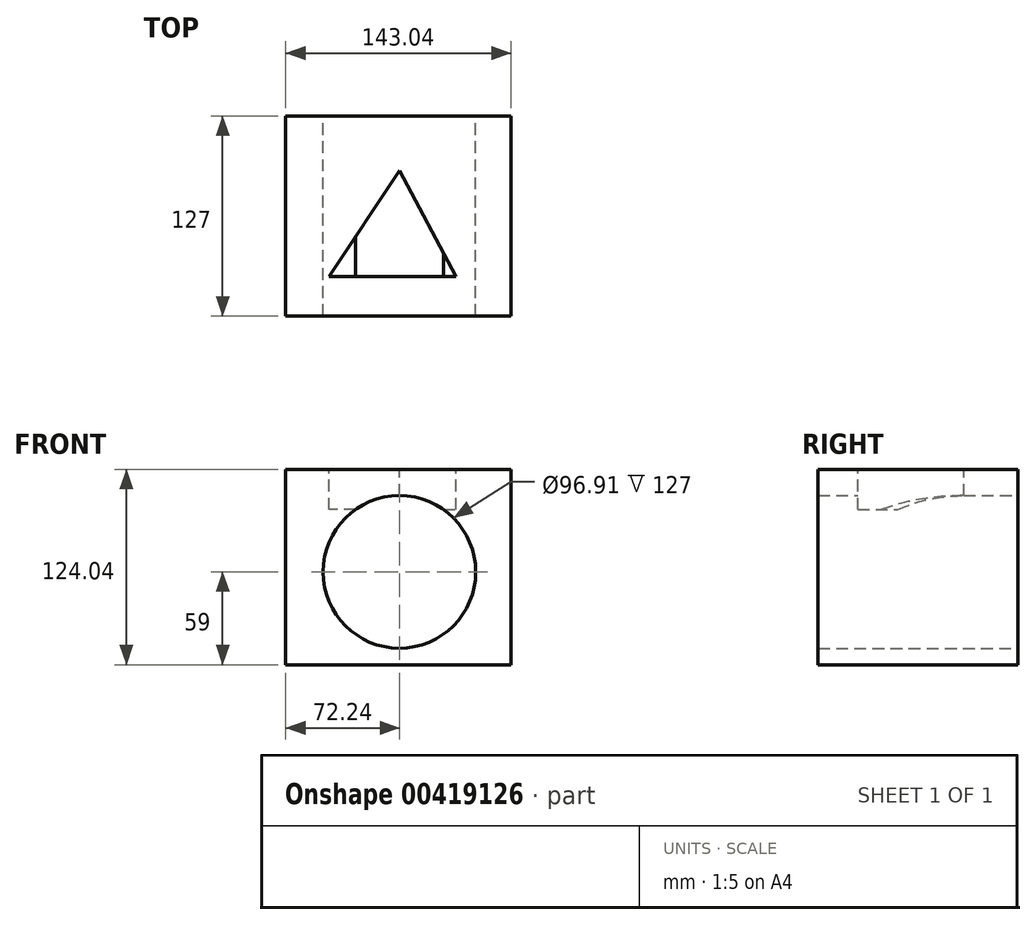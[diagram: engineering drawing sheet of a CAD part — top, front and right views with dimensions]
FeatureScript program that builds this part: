
annotation { "Feature Type Name" : "Feature", "Feature Type Description" : "" }
export const myFeature = defineFeature(function(context is Context, id is Id, definition is map)
    precondition{}
    {
        {
            var Q0;
            Q0=qCreatedBy(makeId("Front.planeOp"),FACE);
            var sketch = newSketch(context, id + "F0", { "sketchPlane" : qUnion([Q0])});
            skLineSegment(sketch, "E0.bottom", {"start": v(-72.24, 65.04) * mm, "end": v(70.8, 65.04) * mm});
            skLineSegment(sketch, "E0.top", {"start": v(-72.24, -59) * mm, "end": v(70.8, -59) * mm});
            skLineSegment(sketch, "E0.left", {"start": v(-72.24, 65.04) * mm, "end": v(-72.24, -59) * mm});
            skLineSegment(sketch, "E0.right", {"start": v(70.8, 65.04) * mm, "end": v(70.8, -59) * mm});
            skCircle(sketch, "E1", {"center": v(0, 0) * mm, "radius": 48.46 * mm});
            skSolve(sketch);
        }
        {
            var Q0;
            Q0=makeQuery(id+"F0.imprint","IMPRINT",FACE,{"disambiguationData":[TD([[makeQuery(id+"F0.imprint","IMPRINT",EDGE,{"derivedFrom":sQuery(id+"F0.wireOp",EDGE,"E0.bottom")}),-1.0]])]});
            extrude(context, id + "F1", {"entities" : qUnion([Q0]), "depth" : 127 * mm});
        }
        {
            var Q0;
            Q0=makeQuery(id+"F1.opExtrude","SWEPT_FACE",FACE,{"disambiguationData":[OSD([sQuery(id+"F0.wireOp",EDGE,"E0.bottom")])]});
            var sketch = newSketch(context, id + "F2", { "sketchPlane" : qUnion([Q0])});
            skLineSegment(sketch, "E2", {"start": v(0, -34.52) * mm, "end": v(-44.86, -101.84) * mm});
            skLineSegment(sketch, "E3", {"start": v(-44.86, -101.84) * mm, "end": v(35.84, -101.84) * mm});
            skLineSegment(sketch, "E4", {"start": v(35.84, -101.84) * mm, "end": v(0, -34.52) * mm});
            skSolve(sketch);
        }
        {
            var Q0;
            Q0=makeQuery(id+"F2.imprint","IMPRINT",FACE,{"disambiguationData":[TD([[makeQuery(id+"F2.imprint","IMPRINT",EDGE,{"derivedFrom":sQuery(id+"F2.wireOp",EDGE,"E2")}),1.0]])]});
            extrude(context, id + "F3", {"entities" : qUnion([Q0]), "operationType" : NewBodyOperationType.REMOVE, "oppositeDirection" : true, "depth" : 25.4 * mm});
        }
    });
